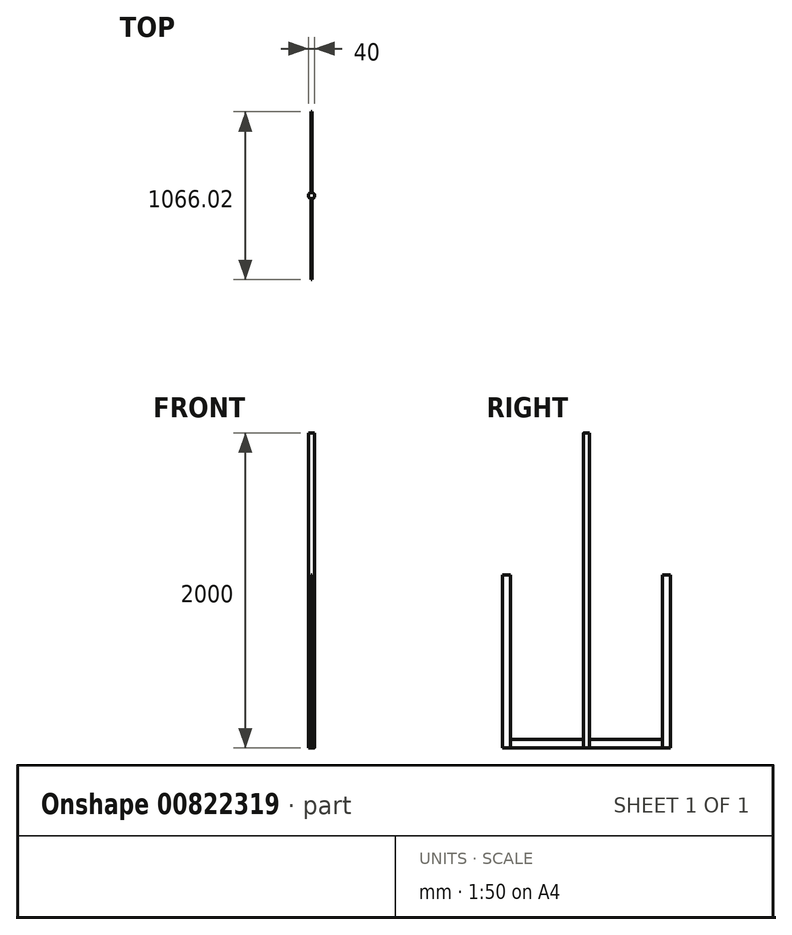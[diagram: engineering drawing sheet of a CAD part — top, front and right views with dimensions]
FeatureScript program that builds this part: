
annotation { "Feature Type Name" : "Feature", "Feature Type Description" : "" }
export const myFeature = defineFeature(function(context is Context, id is Id, definition is map)
    precondition{}
    {
        {
            var Q0;
            Q0=qCreatedBy(makeId("Top.planeOp"),FACE);
            var sketch = newSketch(context, id + "F0", { "sketchPlane" : qUnion([Q0])});
            skCircle(sketch, "E0", {"center": v(0, 0) * mm, "radius": 20 * mm});
            skSolve(sketch);
        }
        {
            var Q0;
            Q0=makeQuery(id+"F0.imprint","IMPRINT",FACE,{"disambiguationData":[TD([[makeQuery(id+"F0.imprint","IMPRINT",EDGE,{"derivedFrom":sQuery(id+"F0.wireOp",EDGE,"E0")}),1.0]])]});
            extrude(context, id + "F1", {"entities" : qUnion([Q0]), "depth" : 2000 * mm, "offsetDistance" : 25 * mm});
        }
        {
            var Q0;
            Q0=qCreatedBy(makeId("Right.planeOp"),FACE);
            var sketch = newSketch(context, id + "F2", { "sketchPlane" : qUnion([Q0])});
            skLineSegment(sketch, "E1", {"start": v(0, 0) * mm, "end": v(-482.93, 0) * mm});
            skLineSegment(sketch, "E2", {"start": v(-482.93, 0) * mm, "end": v(-482.93, 53.33) * mm});
            skLineSegment(sketch, "E3", {"start": v(-482.93, 53.33) * mm, "end": v(0, 53.33) * mm});
            skLineSegment(sketch, "E4", {"start": v(0, 53.33) * mm, "end": v(0, 0) * mm});
            skLineSegment(sketch, "E5.MirrorCS", {"start": v(482.93, 53.33) * mm, "end": v(0, 53.33) * mm});
            skLineSegment(sketch, "E6.MirrorCS", {"start": v(0, 0) * mm, "end": v(482.93, 0) * mm});
            skLineSegment(sketch, "E7.MirrorCS", {"start": v(482.93, 0) * mm, "end": v(482.93, 53.33) * mm});
            skSolve(sketch);
        }
        {
            var Q0;
            Q0 = qSketchRegion(id + "F2", true);
            extrude(context, id + "F3", {"entities" : qUnion([Q0]), "operationType" : NewBodyOperationType.ADD, "depth" : 2.5 * mm, "offsetDistance" : 25 * mm});
        }
        {
            var Q0;
            Q0 = qSketchRegion(id + "F2", true);
            extrude(context, id + "F4", {"entities" : qUnion([Q0]), "operationType" : NewBodyOperationType.ADD, "oppositeDirection" : true, "depth" : 2.5 * mm, "offsetDistance" : 25 * mm});
        }
        {
            var Q0;
            Q0=qCreatedBy(makeId("Right.planeOp"),FACE);
            var sketch = newSketch(context, id + "F5", { "sketchPlane" : qUnion([Q0])});
            skLineSegment(sketch, "E8", {"start": v(-483.01, 0) * mm, "end": v(-483.01, 1100) * mm});
            skLineSegment(sketch, "E9", {"start": v(-483.01, 1100) * mm, "end": v(-533.01, 1100) * mm});
            skLineSegment(sketch, "E10.0", {"start": v(-533.01, 0) * mm, "end": v(-533.01, 1100) * mm});
            skLineSegment(sketch, "E11", {"start": v(-533.01, 0) * mm, "end": v(-483.01, 0) * mm});
            skSolve(sketch);
        }
        {
            var Q0;
            Q0=makeQuery(id+"F5.imprint","IMPRINT",FACE,{"disambiguationData":[TD([[makeQuery(id+"F5.imprint","IMPRINT",EDGE,{"derivedFrom":sQuery(id+"F5.wireOp",EDGE,"E8")}),1.0]])]});
            extrude(context, id + "F6", {"entities" : qUnion([Q0]), "depth" : 2.5 * mm, "offsetDistance" : 25 * mm});
        }
        {
            var Q0;
            Q0=makeQuery(id+"F6.opExtrude","CAP_FACE",FACE,{"disambiguationData":[OSD([sQuery(id+"F5.wireOp",EDGE,"E8"),sQuery(id+"F5.wireOp",EDGE,"E9"),sQuery(id+"F5.wireOp",EDGE,"E10.0"),sQuery(id+"F5.wireOp",EDGE,"E11")])],"isStart":false});
            extrude(context, id + "F7", {"entities" : qUnion([Q0]), "operationType" : NewBodyOperationType.ADD, "oppositeDirection" : true, "depth" : 2.5 * mm, "offsetDistance" : 25 * mm});
        }
        {
            var Q0;
            Q0 = qSketchRegion(id + "F5", true);
            extrude(context, id + "F8", {"entities" : qUnion([Q0]), "operationType" : NewBodyOperationType.ADD, "oppositeDirection" : true, "depth" : 2.5 * mm, "offsetDistance" : 25 * mm});
        }
        {
            var Q0;
            Q0=makeQuery(id+"F6.opExtrude","SWEPT_BODY",BODY,{"disambiguationData":[OSD([sQuery(id+"F5.wireOp",EDGE,"E8"),sQuery(id+"F5.wireOp",EDGE,"E9"),sQuery(id+"F5.wireOp",EDGE,"E10.0"),sQuery(id+"F5.wireOp",EDGE,"E11")])]});
            var Q1;
            Q1=qCreatedBy(makeId("Front.planeOp"),FACE);
            mirror(context, id + "F9", {"entities" : qUnion([Q0]), "mirrorPlane" : qUnion([Q1])});
        }
    });
